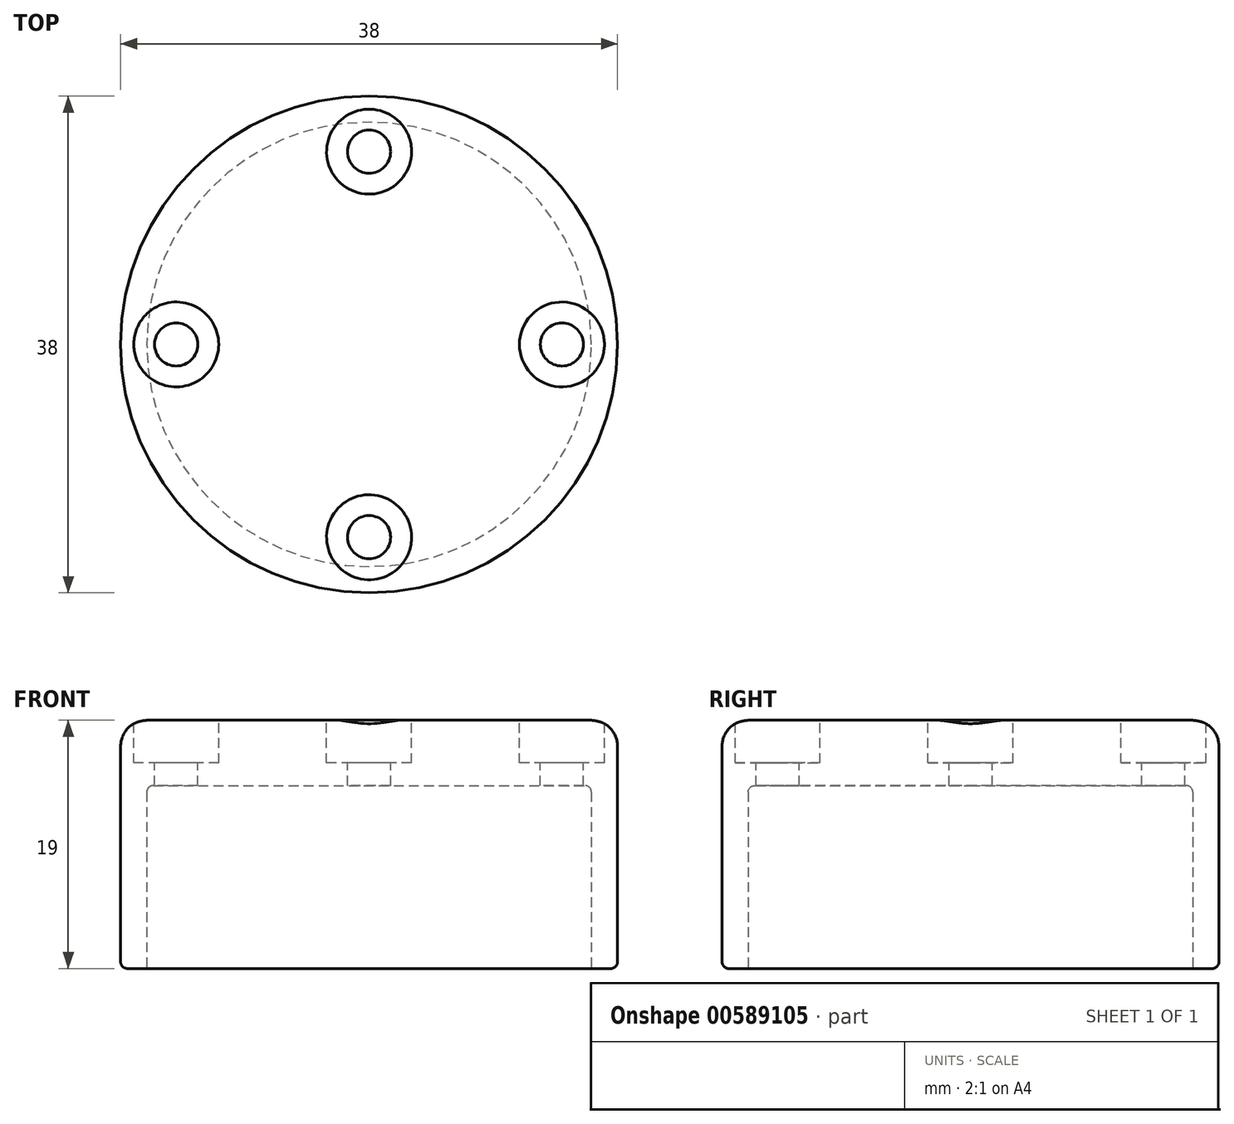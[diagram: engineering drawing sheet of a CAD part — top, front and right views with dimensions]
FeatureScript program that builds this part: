
annotation { "Feature Type Name" : "Feature", "Feature Type Description" : "" }
export const myFeature = defineFeature(function(context is Context, id is Id, definition is map)
    precondition{}
    {
        {
            var Q0;
            Q0=qCreatedBy(makeId("Front.planeOp"),FACE);
            var sketch = newSketch(context, id + "F0", { "sketchPlane" : qUnion([Q0])});
            skLineSegment(sketch, "E0", {"start": v(0, 0) * mm, "end": v(0, 5) * mm});
            skLineSegment(sketch, "E1", {"start": v(0, 5) * mm, "end": v(-17, 5) * mm});
            skLineSegment(sketch, "E2", {"start": v(-19, 3) * mm, "end": v(-19, -13.5) * mm});
            skLineSegment(sketch, "E3", {"start": v(-18.5, -14) * mm, "end": v(-17, -14) * mm});
            skLineSegment(sketch, "E4", {"start": v(-17, -14) * mm, "end": v(-17, -0.5) * mm});
            skLineSegment(sketch, "E5", {"start": v(-16.5, 0) * mm, "end": v(0, 0) * mm});
            skPoint(sketch, "E6.visualSharp", {"position": v(-17, 0) * mm});
            skArc(sketch, "E6.filletArc", {"start": v(-16.5, 0) * mm, "mid": v(-16.85, -0.15) * mm, "end": v(-17, -0.5) * mm});
            skPoint(sketch, "E7.visualSharp", {"position": v(-19, 5) * mm});
            skArc(sketch, "E7.filletArc", {"start": v(-17, 5) * mm, "mid": v(-18.41, 4.41) * mm, "end": v(-19, 3) * mm});
            skPoint(sketch, "E8.visualSharp", {"position": v(-19, -14) * mm});
            skArc(sketch, "E8.filletArc", {"start": v(-19, -13.5) * mm, "mid": v(-18.85, -13.85) * mm, "end": v(-18.5, -14) * mm});
            skSolve(sketch);
        }
        {
            var Q0;
            Q0 = qSketchRegion(id + "F0", true);
            var Q1;
            Q1=sQuery(id+"F0.wireOp",EDGE,"E0");
            revolve(context, id + "F1", {"entities" : qUnion([Q0]), "axis" : qUnion([Q1]), "revolveType" : RevolveType.FULL});
        }
        {
            var Q0;
            Q0=makeQuery(id+"F1.opRevolve","SWEPT_FACE",FACE,{"disambiguationData":[OSD([sQuery(id+"F0.wireOp",EDGE,"E1")])]});
            var sketch = newSketch(context, id + "F2", { "sketchPlane" : qUnion([Q0])});
            skLineSegment(sketch, "E9", {"start": v(0, 14.75) * mm, "end": v(0, -14.75) * mm, "construction": true});
            skLineSegment(sketch, "E10", {"start": v(14.75, 0) * mm, "end": v(-14.75, 0) * mm, "construction": true});
            skSolve(sketch);
        }
        {
            var Q0;
            Q0=sQuery(id+"F2.wireOp",VERTEX,"E9.start");
            var Q1;
            Q1=sQuery(id+"F2.wireOp",VERTEX,"E10.start");
            var Q2;
            Q2=sQuery(id+"F2.wireOp",VERTEX,"E9.end");
            var Q3;
            Q3=sQuery(id+"F2.wireOp",VERTEX,"E10.end");
            var Q4;
            Q4=makeQuery(id+"F1.opRevolve","SWEPT_BODY",BODY,{"disambiguationData":[OSD([sQuery(id+"F0.wireOp",EDGE,"E0"),sQuery(id+"F0.wireOp",EDGE,"E1"),sQuery(id+"F0.wireOp",EDGE,"E2"),sQuery(id+"F0.wireOp",EDGE,"E3"),sQuery(id+"F0.wireOp",EDGE,"E4"),sQuery(id+"F0.wireOp",EDGE,"E5"),sQuery(id+"F0.wireOp",EDGE,"E6.filletArc"),sQuery(id+"F0.wireOp",EDGE,"E7.filletArc"),sQuery(id+"F0.wireOp",EDGE,"E8.filletArc")])]});
            hole(context, id + "F3", {"style" : HoleStyle.C_BORE, "endStyle" : HoleEndStyle.BLIND, "standardTappedOrClearance" : lookupTablePath({ "standard" : "ISO", "fit" : "Normal", "size" : "M3", "type" : "Clearance" }), "standardBlindInLast" : lookupTablePath({ "fit" : "Standard", "standard" : "ISO", "size" : "M3", "type" : "Clearance" }), "holeDiameter" : 3.3 * mm, "cBoreDiameter" : 6.5 * mm, "cBoreDepth" : 3 * mm, "majorDiameter" : 3 * mm, "holeDepth" : 8 * mm, "isTappedThrough" : true, "tappedDepth" : 6.5 * mm, "tapClearance" : 3, "locations" : qUnion([Q0, Q1, Q2, Q3]), "scope" : qUnion([Q4])});
        }
    });
